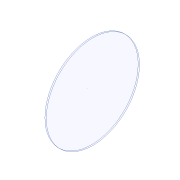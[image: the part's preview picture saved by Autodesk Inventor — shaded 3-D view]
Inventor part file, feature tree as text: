
AUTODESK INVENTOR PART (.ipt)
format: ipt  version: 2020.3 (Build 243373010, 373A)  size: 122,880 bytes
history: native  units: mm
features: revolve x1, sketch x1
ambient origin geometry x8: Origin, YZ Plane, XZ Plane, XY Plane, X Axis, Y Axis, Z Axis, Center Point
bodies: Solid1 (feature_tree)
feature tree (2):
  revolve  "Revolution1"  [1 undecoded]
  sketch  "Sketch1"  dims[d0=35.0mm d1=1.0mm d2=70.0mm d3=200.0mm d4=90.0deg]
note: 1 required parameter value undecoded (feature->parameter linkage not recoverable at this tier; creation-order binding heuristic only, values carry confidence <= 0.55)
